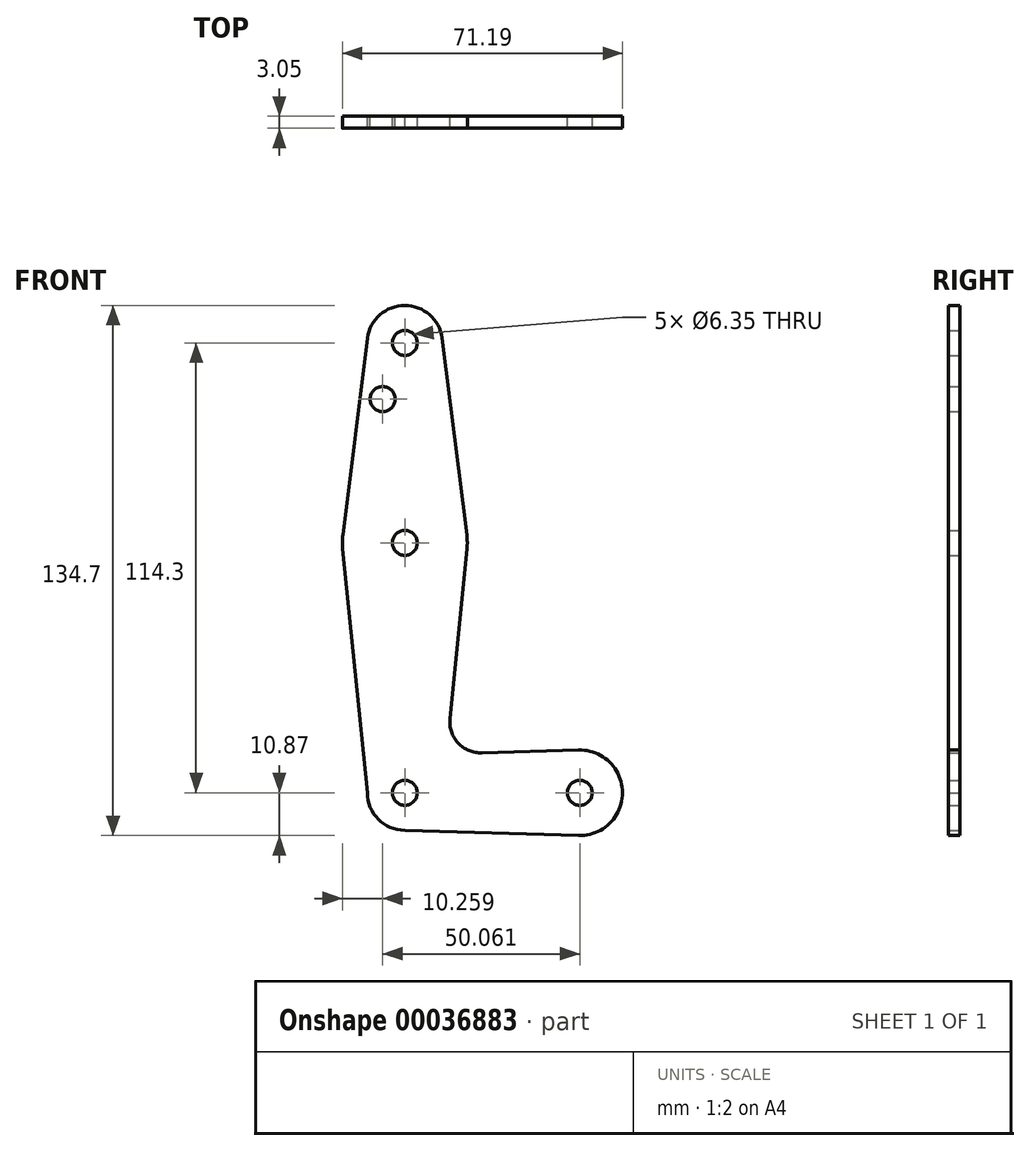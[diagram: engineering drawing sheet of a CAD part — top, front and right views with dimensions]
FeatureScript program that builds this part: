
annotation { "Feature Type Name" : "Feature", "Feature Type Description" : "" }
export const myFeature = defineFeature(function(context is Context, id is Id, definition is map)
    precondition{}
    {
        {
            var Q0;
            Q0=qCreatedBy(makeId("Front.planeOp"),FACE);
            var sketch = newSketch(context, id + "F0", { "sketchPlane" : qUnion([Q0])});
            skLineSegment(sketch, "E0", {"start": v(0, 0) * mm, "end": v(0, 114.3) * mm});
            skLineSegment(sketch, "E1", {"start": v(0, 0) * mm, "end": v(44.45, 0) * mm});
            skCircle(sketch, "E2", {"center": v(0, 114.3) * mm, "radius": 9.53 * mm});
            skCircle(sketch, "E3", {"center": v(0, 0) * mm, "radius": 9.53 * mm});
            skCircle(sketch, "E4", {"center": v(0, 63.5) * mm, "radius": 15.88 * mm});
            skCircle(sketch, "E5", {"center": v(44.45, 0) * mm, "radius": 10.87 * mm});
            skLineSegment(sketch, "E6", {"start": v(-9.45, 115.5) * mm, "end": v(-15.75, 65.48) * mm});
            skLineSegment(sketch, "E7", {"start": v(11.47, 18.86) * mm, "end": v(15.8, 61.91) * mm});
            skLineSegment(sketch, "E8", {"start": v(44.12, 10.86) * mm, "end": v(19.62, 10.12) * mm});
            skPoint(sketch, "E9.startSnap0", {"position": v(0, 57.15) * mm});
            skLineSegment(sketch, "E10", {"start": v(15.75, 65.48) * mm, "end": v(9.45, 115.5) * mm});
            skLineSegment(sketch, "E11", {"start": v(-9.52, 0) * mm, "end": v(-15.8, 61.9) * mm});
            skLineSegment(sketch, "E12", {"start": v(0, -9.53) * mm, "end": v(44.12, -10.86) * mm});
            skCircle(sketch, "E13", {"center": v(0, 114.3) * mm, "radius": 3.18 * mm});
            skCircle(sketch, "E14", {"center": v(0, 63.5) * mm, "radius": 3.18 * mm});
            skCircle(sketch, "E15", {"center": v(0, 0) * mm, "radius": 3.18 * mm});
            skCircle(sketch, "E16", {"center": v(44.45, 0) * mm, "radius": 3.18 * mm});
            skCircle(sketch, "E17", {"center": v(-5.61, 100.03) * mm, "radius": 3.18 * mm});
            skArc(sketch, "E18.filletArc", {"start": v(11.47, 18.86) * mm, "mid": v(13.56, 12.65) * mm, "end": v(19.62, 10.12) * mm});
            skSolve(sketch);
        }
        {
            var Q0;
            Q0 = qSketchRegion(id + "F0", true);
            var Q1;
            {var subQ0=sQuery(id+"F0.wireOp",EDGE,"E15");var subQ3=sQuery(id+"F0.wireOp",EDGE,"E0");var subQ4=makeQuery(id+"F0.imprint","INTERSECT",VERTEX,{"derivedFrom":[subQ3,subQ0]});Q1=makeQuery(id+"F0.imprint","IMPRINT",FACE,{"disambiguationData":[TD([[makeQuery(id+"F0.imprint","IMPRINT",EDGE,{"disambiguationData":[TD([[subQ4,-1.0]])],"derivedFrom":subQ3}),-1.0]])]});}
            extrude(context, id + "F1", {"entities" : qUnion([Q0, Q1]), "depth" : 3.05 * mm});
        }
    });
